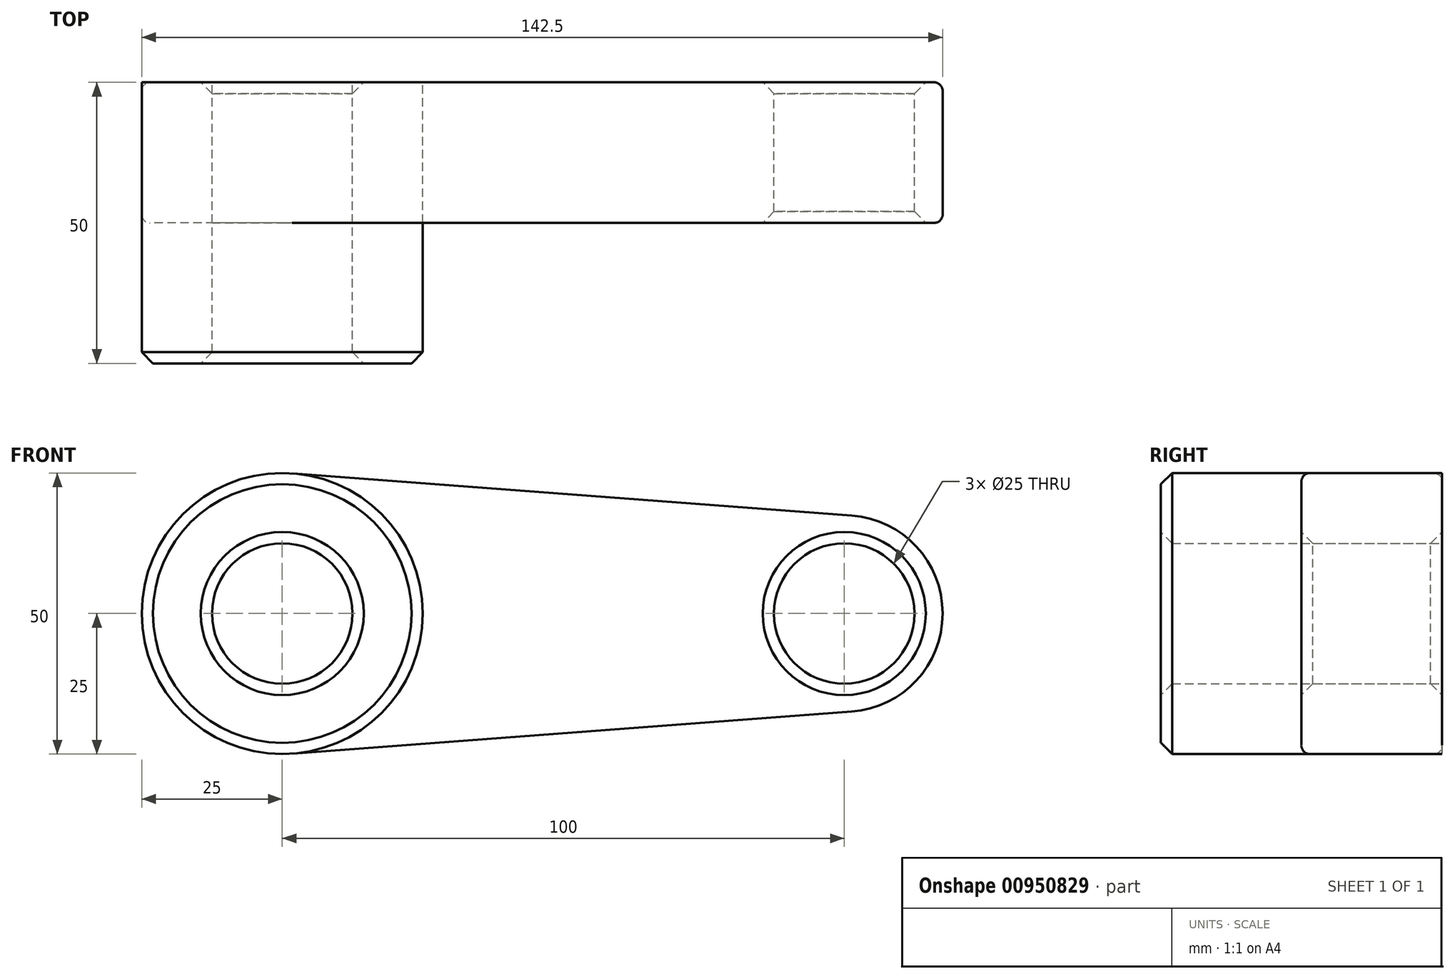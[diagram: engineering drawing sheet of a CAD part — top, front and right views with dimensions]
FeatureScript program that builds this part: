
annotation { "Feature Type Name" : "Feature", "Feature Type Description" : "" }
export const myFeature = defineFeature(function(context is Context, id is Id, definition is map)
    precondition{}
    {
        {
            var Q0;
            Q0=qCreatedBy(makeId("Front.planeOp"),FACE);
            var sketch = newSketch(context, id + "F0", { "sketchPlane" : qUnion([Q0])});
            skCircle(sketch, "E0", {"center": v(0, 0) * mm, "radius": 25 * mm});
            skCircle(sketch, "E1", {"center": v(100, 0) * mm, "radius": 17.5 * mm});
            skLineSegment(sketch, "E2", {"start": v(1.88, 24.93) * mm, "end": v(101.31, 17.45) * mm});
            skLineSegment(sketch, "E3", {"start": v(1.88, -24.93) * mm, "end": v(101.31, -17.45) * mm});
            skCircle(sketch, "E4", {"center": v(0, 0) * mm, "radius": 12.5 * mm});
            skCircle(sketch, "E5", {"center": v(100, 0) * mm, "radius": 12.5 * mm});
            skSolve(sketch);
        }
        {
            var Q0;
            Q0=makeQuery(id+"F0.imprint","IMPRINT",FACE,{"disambiguationData":[TD([[makeQuery(id+"F0.imprint","IMPRINT",EDGE,{"derivedFrom":sQuery(id+"F0.wireOp",EDGE,"E5")}),-1.0]])]});
            var Q1;
            Q1=makeQuery(id+"F0.imprint","IMPRINT",FACE,{"disambiguationData":[TD([[makeQuery(id+"F0.imprint","IMPRINT",EDGE,{"derivedFrom":sQuery(id+"F0.wireOp",EDGE,"E4")}),-1.0]])]});
            var Q2;
            {var subQ0=sQuery(id+"F0.wireOp",EDGE,"E2");Q2=makeQuery(id+"F0.imprint","IMPRINT",FACE,{"disambiguationData":[TD([[makeQuery(id+"F0.imprint","IMPRINT",EDGE,{"derivedFrom":subQ0}),-1.0]])]});}
            extrude(context, id + "F1", {"entities" : qUnion([Q0, Q1, Q2]), "depth" : 25 * mm, "offsetDistance" : 25 * mm});
        }
        {
            var Q0;
            Q0=makeQuery(id+"F0.imprint","IMPRINT",FACE,{"disambiguationData":[TD([[makeQuery(id+"F0.imprint","IMPRINT",EDGE,{"derivedFrom":sQuery(id+"F0.wireOp",EDGE,"E4")}),-1.0]])]});
            extrude(context, id + "F2", {"entities" : qUnion([Q0]), "depth" : 50 * mm, "offsetDistance" : 25 * mm});
        }
        {
            var Q0;
            Q0=makeQuery(id+"F2.opExtrude","SWEPT_FACE",FACE,{"disambiguationData":[OSD([sQuery(id+"F0.wireOp",EDGE,"E4")])]});
            chamfer(context, id + "F3", {"entities" : qUnion([Q0]), "width" : 2 * mm, "tangentPropagation" : true});
        }
        {
            var Q0;
            Q0=makeQuery(id+"F2.opExtrude","CAP_EDGE",EDGE,{"disambiguationData":[OSD([sQuery(id+"F0.wireOp",EDGE,"E0")])],"isStart":false});
            chamfer(context, id + "F4", {"entities" : qUnion([Q0]), "width" : 2 * mm, "tangentPropagation" : true});
        }
        {
            var Q0;
            Q0=makeQuery(id+"F1.opExtrude","CAP_EDGE",EDGE,{"disambiguationData":[OSD([sQuery(id+"F0.wireOp",EDGE,"E5")])],"isStart":false});
            var Q1;
            Q1=makeQuery(id+"F1.opExtrude","SWEPT_FACE",FACE,{"disambiguationData":[OSD([sQuery(id+"F0.wireOp",EDGE,"E5")])]});
            chamfer(context, id + "F5", {"entities" : qUnion([Q0, Q1]), "width" : 2 * mm, "tangentPropagation" : true});
        }
        {
            var Q0;
            Q0=makeQuery(id+"F1.opExtrude","CAP_EDGE",EDGE,{"disambiguationData":[OSD([sQuery(id+"F0.wireOp",EDGE,"E2")])],"isStart":false});
            var Q1;
            Q1=makeQuery(id+"F1.opExtrude","CAP_EDGE",EDGE,{"disambiguationData":[OSD([sQuery(id+"F0.wireOp",EDGE,"E2")])],"isStart":true});
            fillet(context, id + "F6", {"entities" : qUnion([Q0, Q1]), "radius" : 1.5 * mm, "tangentPropagation" : true, "allowEdgeOverflow" : false});
        }
    });
